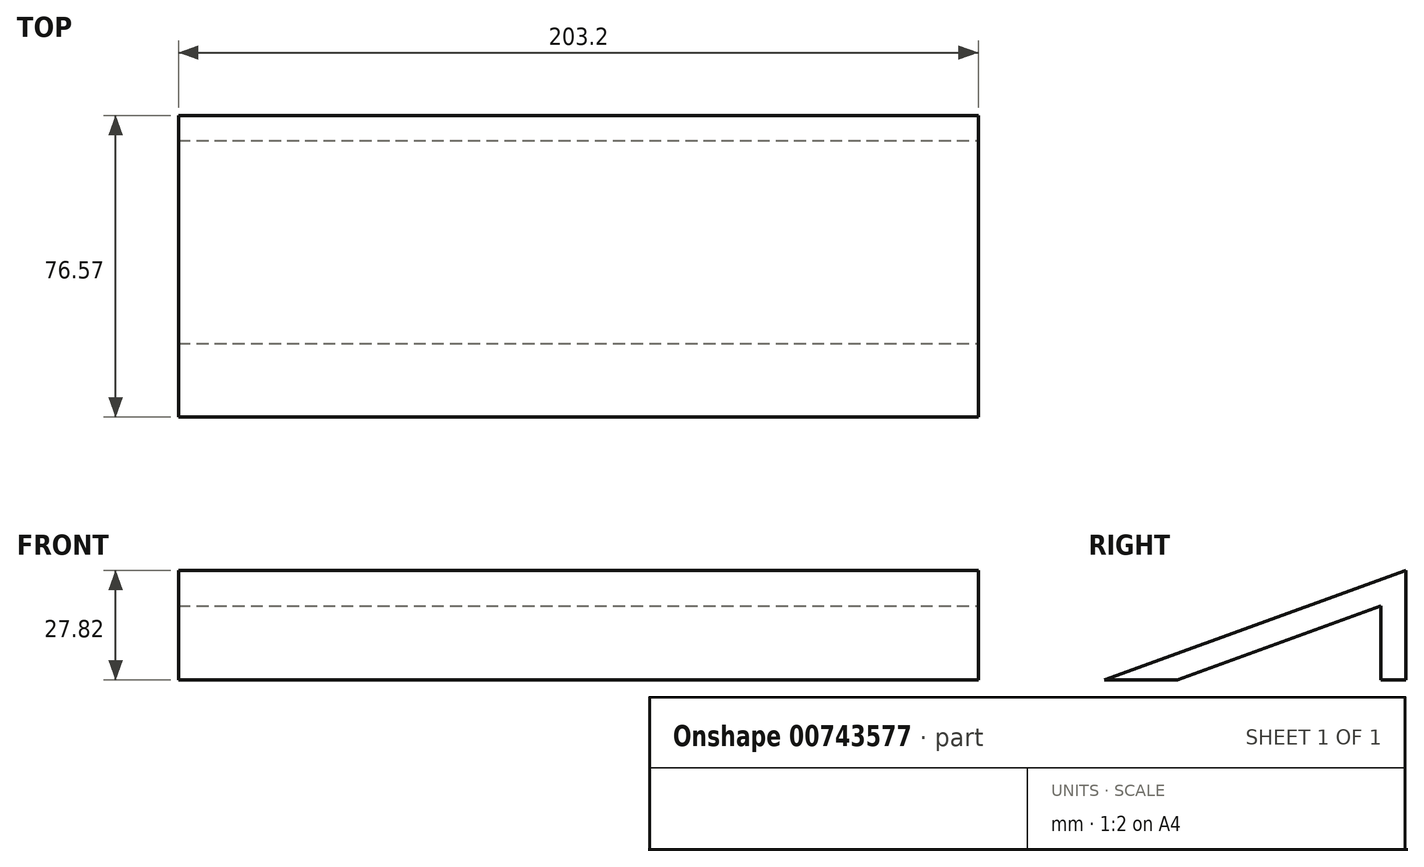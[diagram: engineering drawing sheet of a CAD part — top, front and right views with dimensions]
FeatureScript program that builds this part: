
annotation { "Feature Type Name" : "Feature", "Feature Type Description" : "" }
export const myFeature = defineFeature(function(context is Context, id is Id, definition is map)
    precondition{}
    {
        {
            var Q0;
            Q0=qCreatedBy(makeId("Top.planeOp"),FACE);
            var sketch = newSketch(context, id + "F0", { "sketchPlane" : qUnion([Q0])});
            skLineSegment(sketch, "E0.bottom", {"start": v(-26.36, 24.86) * mm, "end": v(32.58, 24.86) * mm});
            skLineSegment(sketch, "E0.top", {"start": v(-26.36, -24.51) * mm, "end": v(32.58, -24.51) * mm});
            skLineSegment(sketch, "E0.left", {"start": v(-26.36, 24.86) * mm, "end": v(-26.36, -24.51) * mm});
            skLineSegment(sketch, "E0.right", {"start": v(32.58, 24.86) * mm, "end": v(32.58, -24.51) * mm});
            skSolve(sketch);
        }
        {
            var Q0;
            Q0 = qSketchRegion(id + "F0", true);
            extrude(context, id + "F1", {"entities" : qUnion([Q0]), "depth" : 134.75 * mm, "offsetDistance" : 25.4 * mm});
        }
        {
            var Q0;
            Q0=makeQuery(id+"F1.opExtrude","SWEPT_FACE",FACE,{"disambiguationData":[OSD([sQuery(id+"F0.wireOp",EDGE,"E0.left")])]});
            var sketch = newSketch(context, id + "F2", { "sketchPlane" : qUnion([Q0])});
            skCircle(sketch, "E1", {"center": v(10.27, 109.35) * mm, "radius": 16.97 * mm});
            skSolve(sketch);
        }
        {
            var Q0;
            Q0 = qSketchRegion(id + "F2", true);
            extrude(context, id + "F3", {"entities" : qUnion([Q0]), "operationType" : NewBodyOperationType.REMOVE, "endBound" : BoundingType.THROUGH_ALL, "oppositeDirection" : true, "depth" : 25.4 * mm, "offsetDistance" : 25.4 * mm});
        }
        {
            var Q0;
            Q0=makeQuery(id+"F1.opExtrude","CAP_EDGE",EDGE,{"disambiguationData":[OSD([sQuery(id+"F0.wireOp",EDGE,"E0.right")])],"isStart":false});
            fillet(context, id + "F4", {"entities" : qUnion([Q0]), "radius" : 12.7 * mm, "tangentPropagation" : true, "allowEdgeOverflow" : false});
        }
        {
            var Q0;
            Q0=makeQuery(id+"F1.opExtrude","SWEPT_BODY",BODY,{"disambiguationData":[OSD([sQuery(id+"F0.wireOp",EDGE,"E0.bottom"),sQuery(id+"F0.wireOp",EDGE,"E0.top"),sQuery(id+"F0.wireOp",EDGE,"E0.left"),sQuery(id+"F0.wireOp",EDGE,"E0.right")])]});
            deleteBodies(context, id + "F5", {"entities" : qUnion([Q0])});
        }
        {
            var Q0;
            Q0=qCreatedBy(makeId("Right.planeOp"),FACE);
            var sketch = newSketch(context, id + "F6", { "sketchPlane" : qUnion([Q0])});
            skLineSegment(sketch, "E2", {"start": v(33.28, 43.15) * mm, "end": v(33.28, 15.33) * mm});
            skLineSegment(sketch, "E3", {"start": v(33.28, 15.33) * mm, "end": v(-43.29, 15.33) * mm});
            skLineSegment(sketch, "E4", {"start": v(-43.29, 15.33) * mm, "end": v(33.28, 43.15) * mm});
            skSolve(sketch);
        }
        {
            var Q0;
            Q0=makeQuery(id+"F6.imprint","IMPRINT",FACE,{"disambiguationData":[TD([[makeQuery(id+"F6.imprint","IMPRINT",EDGE,{"derivedFrom":sQuery(id+"F6.wireOp",EDGE,"E2")}),-1.0]])]});
            extrude(context, id + "F7", {"entities" : qUnion([Q0]), "depth" : 203.2 * mm, "offsetDistance" : 25.4 * mm});
        }
        {
            var Q0;
            Q0=makeQuery(id+"F7.opExtrude","CAP_FACE",FACE,{"disambiguationData":[OSD([sQuery(id+"F6.wireOp",EDGE,"E2"),sQuery(id+"F6.wireOp",EDGE,"E3"),sQuery(id+"F6.wireOp",EDGE,"E4")])],"isStart":false});
            var sketch = newSketch(context, id + "F8", { "sketchPlane" : qUnion([Q0])});
            skLineSegment(sketch, "E5.0", {"start": v(-24.7, 15.33) * mm, "end": v(26.93, 34.09) * mm});
            skLineSegment(sketch, "E6.0", {"start": v(26.93, 34.09) * mm, "end": v(26.93, 15.33) * mm});
            skLineSegment(sketch, "E7", {"start": v(26.93, 15.33) * mm, "end": v(-24.7, 15.33) * mm});
            skSolve(sketch);
        }
        {
            var Q0;
            Q0 = qSketchRegion(id + "F8", true);
            extrude(context, id + "F9", {"entities" : qUnion([Q0]), "operationType" : NewBodyOperationType.REMOVE, "endBound" : BoundingType.THROUGH_ALL, "oppositeDirection" : true, "depth" : 25.4 * mm, "offsetDistance" : 25.4 * mm});
        }
    });
